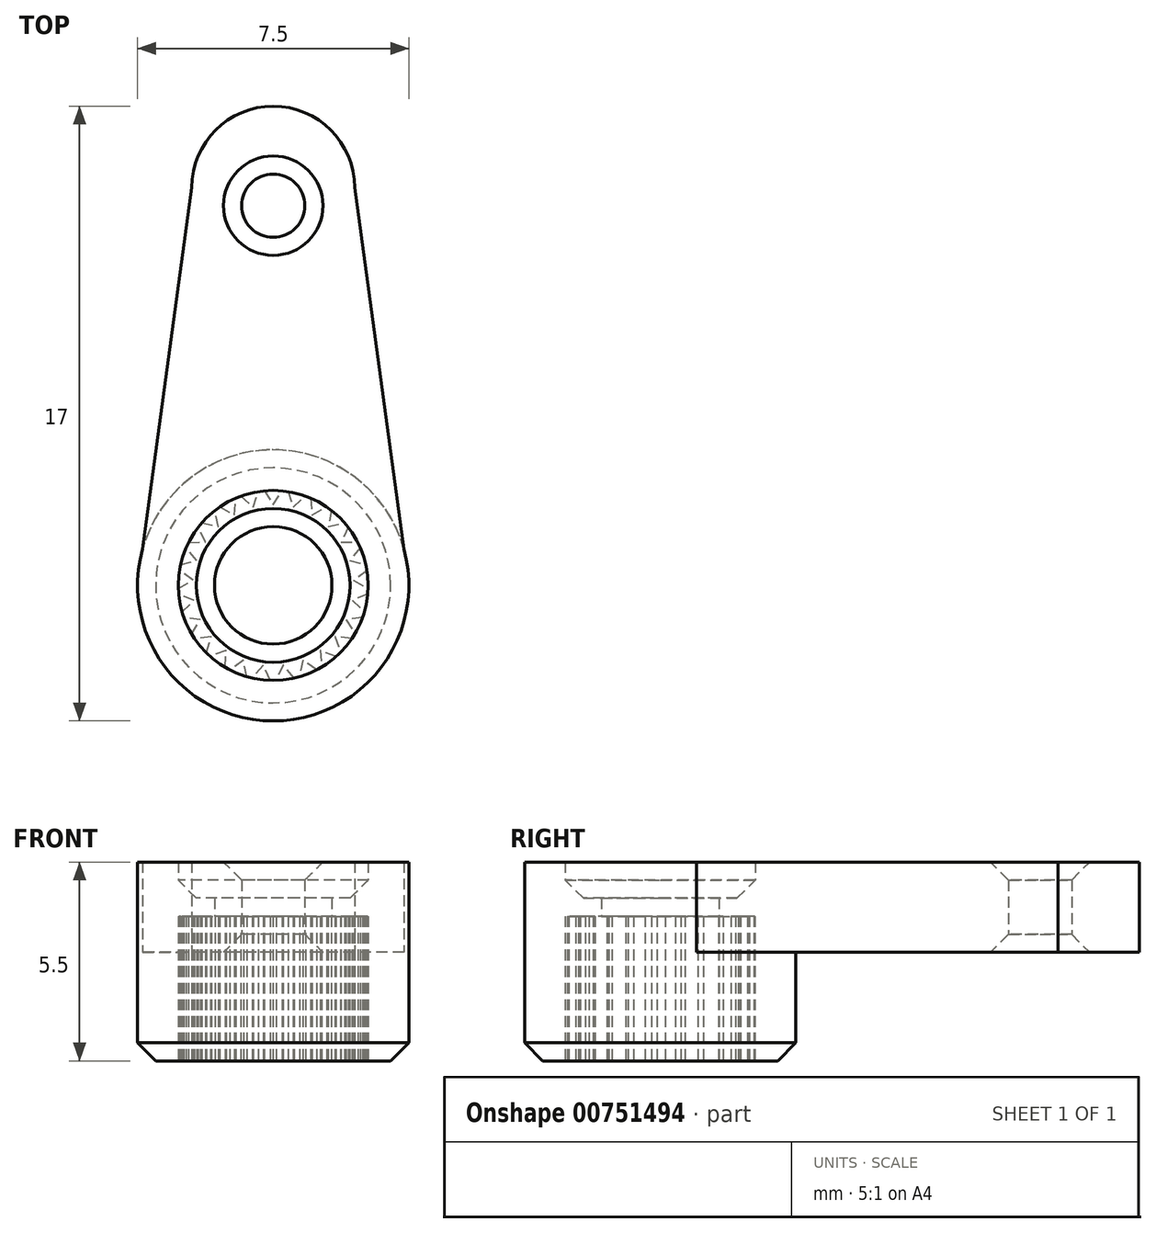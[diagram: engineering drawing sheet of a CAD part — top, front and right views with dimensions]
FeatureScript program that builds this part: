
annotation { "Feature Type Name" : "Feature", "Feature Type Description" : "" }
export const myFeature = defineFeature(function(context is Context, id is Id, definition is map)
    precondition{}
    {
        {
            assignVariable(context, id + "F0", {"name" : "BaseHeight", "anyValue" : 4});
        }
        {
            var Q0;
            Q0=qCreatedBy(makeId("Top.planeOp"),FACE);
            var sketch = newSketch(context, id + "F1", { "sketchPlane" : qUnion([Q0])});
            skCircle(sketch, "E0", {"center": v(0, 0) * mm, "radius": 2.62 * mm});
            skCircle(sketch, "E1", {"center": v(0, 0) * mm, "radius": 3.75 * mm});
            skLineSegment(sketch, "E2", {"start": v(-0.25, 2.61) * mm, "end": v(0, 2.23) * mm});
            skLineSegment(sketch, "E3", {"start": v(0, 2.23) * mm, "end": v(0.25, 2.61) * mm});
            skLineSegment(sketch, "E4.1.0", {"start": v(-0.55, 2.16) * mm, "end": v(-0.4, 2.6) * mm});
            skLineSegment(sketch, "E4.1.1", {"start": v(-0.9, 2.47) * mm, "end": v(-0.55, 2.16) * mm});
            skLineSegment(sketch, "E4.2.0", {"start": v(-1.07, 1.95) * mm, "end": v(-1.04, 2.41) * mm});
            skLineSegment(sketch, "E4.2.1", {"start": v(-1.48, 2.17) * mm, "end": v(-1.07, 1.95) * mm});
            skLineSegment(sketch, "E4.3.0", {"start": v(-1.52, 1.62) * mm, "end": v(-1.6, 2.08) * mm});
            skLineSegment(sketch, "E4.3.1", {"start": v(-1.97, 1.73) * mm, "end": v(-1.52, 1.62) * mm});
            skLineSegment(sketch, "E4.4.0", {"start": v(-1.88, 1.2) * mm, "end": v(-2.07, 1.61) * mm});
            skLineSegment(sketch, "E4.4.1", {"start": v(-2.34, 1.19) * mm, "end": v(-1.88, 1.2) * mm});
            skLineSegment(sketch, "E4.5.0", {"start": v(-2.12, 0.69) * mm, "end": v(-2.4, 1.05) * mm});
            skLineSegment(sketch, "E4.5.1", {"start": v(-2.56, 0.57) * mm, "end": v(-2.12, 0.69) * mm});
            skLineSegment(sketch, "E4.6.0", {"start": v(-2.22, 0.14) * mm, "end": v(-2.6, 0.41) * mm});
            skLineSegment(sketch, "E4.6.1", {"start": v(-2.62, -0.09) * mm, "end": v(-2.22, 0.14) * mm});
            skLineSegment(sketch, "E4.7.0", {"start": v(-2.19, -0.42) * mm, "end": v(-2.61, -0.24) * mm});
            skLineSegment(sketch, "E4.7.1", {"start": v(-2.52, -0.74) * mm, "end": v(-2.19, -0.42) * mm});
            skLineSegment(sketch, "E4.8.0", {"start": v(-2.01, -0.95) * mm, "end": v(-2.47, -0.89) * mm});
            skLineSegment(sketch, "E4.8.1", {"start": v(-2.26, -1.34) * mm, "end": v(-2.01, -0.95) * mm});
            skLineSegment(sketch, "E4.9.0", {"start": v(-1.71, -1.42) * mm, "end": v(-2.17, -1.47) * mm});
            skLineSegment(sketch, "E4.9.1", {"start": v(-1.85, -1.86) * mm, "end": v(-1.71, -1.42) * mm});
            skLineSegment(sketch, "E4.10.0", {"start": v(-1.3, -1.8) * mm, "end": v(-1.74, -1.97) * mm});
            skLineSegment(sketch, "E4.10.1", {"start": v(-1.33, -2.26) * mm, "end": v(-1.3, -1.8) * mm});
            skLineSegment(sketch, "E4.11.0", {"start": v(-0.82, -2.07) * mm, "end": v(-1.2, -2.34) * mm});
            skLineSegment(sketch, "E4.11.1", {"start": v(-0.73, -2.52) * mm, "end": v(-0.82, -2.07) * mm});
            skLineSegment(sketch, "E4.12.0", {"start": v(-0.28, -2.2) * mm, "end": v(-0.58, -2.56) * mm});
            skLineSegment(sketch, "E4.12.1", {"start": v(-0.08, -2.62) * mm, "end": v(-0.28, -2.2) * mm});
            skLineSegment(sketch, "E4.13.0", {"start": v(0.28, -2.2) * mm, "end": v(0.08, -2.62) * mm});
            skLineSegment(sketch, "E4.13.1", {"start": v(0.58, -2.56) * mm, "end": v(0.28, -2.2) * mm});
            skLineSegment(sketch, "E4.14.0", {"start": v(0.82, -2.07) * mm, "end": v(0.73, -2.52) * mm});
            skLineSegment(sketch, "E4.14.1", {"start": v(1.2, -2.34) * mm, "end": v(0.82, -2.07) * mm});
            skLineSegment(sketch, "E4.15.0", {"start": v(1.3, -1.8) * mm, "end": v(1.33, -2.26) * mm});
            skLineSegment(sketch, "E4.15.1", {"start": v(1.74, -1.97) * mm, "end": v(1.3, -1.8) * mm});
            skLineSegment(sketch, "E4.16.0", {"start": v(1.71, -1.42) * mm, "end": v(1.85, -1.86) * mm});
            skLineSegment(sketch, "E4.16.1", {"start": v(2.17, -1.47) * mm, "end": v(1.71, -1.42) * mm});
            skLineSegment(sketch, "E4.17.0", {"start": v(2.01, -0.95) * mm, "end": v(2.26, -1.34) * mm});
            skLineSegment(sketch, "E4.17.1", {"start": v(2.47, -0.89) * mm, "end": v(2.01, -0.95) * mm});
            skLineSegment(sketch, "E4.18.0", {"start": v(2.19, -0.42) * mm, "end": v(2.52, -0.74) * mm});
            skLineSegment(sketch, "E4.18.1", {"start": v(2.61, -0.24) * mm, "end": v(2.19, -0.42) * mm});
            skLineSegment(sketch, "E4.19.0", {"start": v(2.22, 0.14) * mm, "end": v(2.62, -0.09) * mm});
            skLineSegment(sketch, "E4.19.1", {"start": v(2.6, 0.41) * mm, "end": v(2.22, 0.14) * mm});
            skLineSegment(sketch, "E4.20.0", {"start": v(2.12, 0.69) * mm, "end": v(2.56, 0.57) * mm});
            skLineSegment(sketch, "E4.20.1", {"start": v(2.4, 1.05) * mm, "end": v(2.12, 0.69) * mm});
            skLineSegment(sketch, "E4.21.0", {"start": v(1.88, 1.2) * mm, "end": v(2.34, 1.19) * mm});
            skLineSegment(sketch, "E4.21.1", {"start": v(2.07, 1.61) * mm, "end": v(1.88, 1.2) * mm});
            skLineSegment(sketch, "E4.22.0", {"start": v(1.52, 1.62) * mm, "end": v(1.97, 1.73) * mm});
            skLineSegment(sketch, "E4.22.1", {"start": v(1.6, 2.08) * mm, "end": v(1.52, 1.62) * mm});
            skLineSegment(sketch, "E4.23.0", {"start": v(1.07, 1.95) * mm, "end": v(1.48, 2.17) * mm});
            skLineSegment(sketch, "E4.23.1", {"start": v(1.04, 2.41) * mm, "end": v(1.07, 1.95) * mm});
            skLineSegment(sketch, "E4.24.0", {"start": v(0.55, 2.16) * mm, "end": v(0.9, 2.47) * mm});
            skLineSegment(sketch, "E4.24.1", {"start": v(0.4, 2.6) * mm, "end": v(0.55, 2.16) * mm});
            skCircle(sketch, "E5", {"center": v(0, 0) * mm, "radius": 1.63 * mm});
            skLineSegment(sketch, "E6", {"start": v(-3.61, 1) * mm, "end": v(-2.25, 11) * mm});
            skLineSegment(sketch, "E7", {"start": v(3.61, 1) * mm, "end": v(2.25, 11) * mm});
            skArc(sketch, "E8", {"start": v(2.25, 11) * mm, "mid": v(0, 13.25) * mm, "end": v(-2.25, 11) * mm});
            skPoint(sketch, "E9.orphan", {"position": v(-3.75, 0) * mm});
            skPoint(sketch, "E10.orphan", {"position": v(3.75, 0) * mm});
            skCircle(sketch, "E11", {"center": v(0, 10.5) * mm, "radius": 0.88 * mm});
            skSolve(sketch);
        }
        {
            var Q0;
            Q0=makeQuery(id+"F1.imprint","IMPRINT",FACE,{"disambiguationData":[TD([[makeQuery(id+"F1.imprint","IMPRINT",EDGE,{"derivedFrom":sQuery(id+"F1.wireOp",EDGE,"E0")}),-1.0]])]});
            extrude(context, id + "F2", {"entities" : qUnion([Q0]), "depth" : (getVariable(context, 'BaseHeight') + 1.5) * mm, "offsetDistance" : 25 * mm});
        }
        {
            var Q0;
            Q0=makeQuery(id+"F2.opExtrude","CAP_FACE",FACE,{"disambiguationData":[OSD([sQuery(id+"F1.wireOp",EDGE,"E0"),sQuery(id+"F1.wireOp",EDGE,"E1")])],"isStart":true});
            var Q1;
            {var subQ0=sQuery(id+"F1.wireOp",EDGE,"0f8284f6-a0f2-4ead-9c26-bed78ff55800.22.0");Q1=makeQuery(id+"F1.imprint","IMPRINT",FACE,{"disambiguationData":[TD([[makeQuery(id+"F1.imprint","IMPRINT",EDGE,{"derivedFrom":subQ0}),1.0]])]});}
            var Q2;
            {var subQ0=sQuery(id+"F1.wireOp",EDGE,"0f8284f6-a0f2-4ead-9c26-bed78ff55800.17.0");Q2=makeQuery(id+"F1.imprint","IMPRINT",FACE,{"disambiguationData":[TD([[makeQuery(id+"F1.imprint","IMPRINT",EDGE,{"derivedFrom":subQ0}),1.0]])]});}
            var Q3;
            {var subQ0=sQuery(id+"F1.wireOp",EDGE,"0f8284f6-a0f2-4ead-9c26-bed78ff55800.10.0");Q3=makeQuery(id+"F1.imprint","IMPRINT",FACE,{"disambiguationData":[TD([[makeQuery(id+"F1.imprint","IMPRINT",EDGE,{"derivedFrom":subQ0}),1.0]])]});}
            var Q4;
            {var subQ0=sQuery(id+"F1.wireOp",EDGE,"0f8284f6-a0f2-4ead-9c26-bed78ff55800.14.0");Q4=makeQuery(id+"F1.imprint","IMPRINT",FACE,{"disambiguationData":[TD([[makeQuery(id+"F1.imprint","IMPRINT",EDGE,{"derivedFrom":subQ0}),1.0]])]});}
            var Q5;
            {var subQ0=sQuery(id+"F1.wireOp",EDGE,"0f8284f6-a0f2-4ead-9c26-bed78ff55800.8.0");Q5=makeQuery(id+"F1.imprint","IMPRINT",FACE,{"disambiguationData":[TD([[makeQuery(id+"F1.imprint","IMPRINT",EDGE,{"derivedFrom":subQ0}),1.0]])]});}
            var Q6;
            {var subQ0=sQuery(id+"F1.wireOp",EDGE,"0f8284f6-a0f2-4ead-9c26-bed78ff55800.6.0");Q6=makeQuery(id+"F1.imprint","IMPRINT",FACE,{"disambiguationData":[TD([[makeQuery(id+"F1.imprint","IMPRINT",EDGE,{"derivedFrom":subQ0}),1.0]])]});}
            var Q7;
            {var subQ0=sQuery(id+"F1.wireOp",EDGE,"0f8284f6-a0f2-4ead-9c26-bed78ff55800.21.0");Q7=makeQuery(id+"F1.imprint","IMPRINT",FACE,{"disambiguationData":[TD([[makeQuery(id+"F1.imprint","IMPRINT",EDGE,{"derivedFrom":subQ0}),1.0]])]});}
            var Q8;
            {var subQ0=sQuery(id+"F1.wireOp",EDGE,"0f8284f6-a0f2-4ead-9c26-bed78ff55800.23.0");Q8=makeQuery(id+"F1.imprint","IMPRINT",FACE,{"disambiguationData":[TD([[makeQuery(id+"F1.imprint","IMPRINT",EDGE,{"derivedFrom":subQ0}),1.0]])]});}
            var Q9;
            {var subQ0=sQuery(id+"F1.wireOp",EDGE,"0f8284f6-a0f2-4ead-9c26-bed78ff55800.24.0");Q9=makeQuery(id+"F1.imprint","IMPRINT",FACE,{"disambiguationData":[TD([[makeQuery(id+"F1.imprint","IMPRINT",EDGE,{"derivedFrom":subQ0}),1.0]])]});}
            var Q10;
            {var subQ0=sQuery(id+"F1.wireOp",EDGE,"E2");Q10=makeQuery(id+"F1.imprint","IMPRINT",FACE,{"disambiguationData":[TD([[makeQuery(id+"F1.imprint","IMPRINT",EDGE,{"derivedFrom":subQ0}),1.0]])]});}
            var Q11;
            {var subQ0=sQuery(id+"F1.wireOp",EDGE,"0f8284f6-a0f2-4ead-9c26-bed78ff55800.2.0");Q11=makeQuery(id+"F1.imprint","IMPRINT",FACE,{"disambiguationData":[TD([[makeQuery(id+"F1.imprint","IMPRINT",EDGE,{"derivedFrom":subQ0}),1.0]])]});}
            var Q12;
            {var subQ0=sQuery(id+"F1.wireOp",EDGE,"0f8284f6-a0f2-4ead-9c26-bed78ff55800.3.0");Q12=makeQuery(id+"F1.imprint","IMPRINT",FACE,{"disambiguationData":[TD([[makeQuery(id+"F1.imprint","IMPRINT",EDGE,{"derivedFrom":subQ0}),1.0]])]});}
            var Q13;
            {var subQ0=sQuery(id+"F1.wireOp",EDGE,"0f8284f6-a0f2-4ead-9c26-bed78ff55800.4.0");Q13=makeQuery(id+"F1.imprint","IMPRINT",FACE,{"disambiguationData":[TD([[makeQuery(id+"F1.imprint","IMPRINT",EDGE,{"derivedFrom":subQ0}),1.0]])]});}
            var Q14;
            {var subQ0=sQuery(id+"F1.wireOp",EDGE,"0f8284f6-a0f2-4ead-9c26-bed78ff55800.19.0");Q14=makeQuery(id+"F1.imprint","IMPRINT",FACE,{"disambiguationData":[TD([[makeQuery(id+"F1.imprint","IMPRINT",EDGE,{"derivedFrom":subQ0}),1.0]])]});}
            var Q15;
            {var subQ0=sQuery(id+"F1.wireOp",EDGE,"0f8284f6-a0f2-4ead-9c26-bed78ff55800.15.0");Q15=makeQuery(id+"F1.imprint","IMPRINT",FACE,{"disambiguationData":[TD([[makeQuery(id+"F1.imprint","IMPRINT",EDGE,{"derivedFrom":subQ0}),1.0]])]});}
            var Q16;
            {var subQ0=sQuery(id+"F1.wireOp",EDGE,"0f8284f6-a0f2-4ead-9c26-bed78ff55800.13.0");Q16=makeQuery(id+"F1.imprint","IMPRINT",FACE,{"disambiguationData":[TD([[makeQuery(id+"F1.imprint","IMPRINT",EDGE,{"derivedFrom":subQ0}),1.0]])]});}
            var Q17;
            {var subQ0=sQuery(id+"F1.wireOp",EDGE,"0f8284f6-a0f2-4ead-9c26-bed78ff55800.18.0");Q17=makeQuery(id+"F1.imprint","IMPRINT",FACE,{"disambiguationData":[TD([[makeQuery(id+"F1.imprint","IMPRINT",EDGE,{"derivedFrom":subQ0}),1.0]])]});}
            var Q18;
            {var subQ0=sQuery(id+"F1.wireOp",EDGE,"0f8284f6-a0f2-4ead-9c26-bed78ff55800.12.0");Q18=makeQuery(id+"F1.imprint","IMPRINT",FACE,{"disambiguationData":[TD([[makeQuery(id+"F1.imprint","IMPRINT",EDGE,{"derivedFrom":subQ0}),1.0]])]});}
            var Q19;
            {var subQ0=sQuery(id+"F1.wireOp",EDGE,"0f8284f6-a0f2-4ead-9c26-bed78ff55800.7.0");Q19=makeQuery(id+"F1.imprint","IMPRINT",FACE,{"disambiguationData":[TD([[makeQuery(id+"F1.imprint","IMPRINT",EDGE,{"derivedFrom":subQ0}),1.0]])]});}
            var Q20;
            {var subQ0=sQuery(id+"F1.wireOp",EDGE,"0f8284f6-a0f2-4ead-9c26-bed78ff55800.5.0");Q20=makeQuery(id+"F1.imprint","IMPRINT",FACE,{"disambiguationData":[TD([[makeQuery(id+"F1.imprint","IMPRINT",EDGE,{"derivedFrom":subQ0}),1.0]])]});}
            var Q21;
            {var subQ0=sQuery(id+"F1.wireOp",EDGE,"0f8284f6-a0f2-4ead-9c26-bed78ff55800.20.0");Q21=makeQuery(id+"F1.imprint","IMPRINT",FACE,{"disambiguationData":[TD([[makeQuery(id+"F1.imprint","IMPRINT",EDGE,{"derivedFrom":subQ0}),1.0]])]});}
            var Q22;
            {var subQ0=sQuery(id+"F1.wireOp",EDGE,"0f8284f6-a0f2-4ead-9c26-bed78ff55800.1.0");Q22=makeQuery(id+"F1.imprint","IMPRINT",FACE,{"disambiguationData":[TD([[makeQuery(id+"F1.imprint","IMPRINT",EDGE,{"derivedFrom":subQ0}),1.0]])]});}
            var Q23;
            {var subQ0=sQuery(id+"F1.wireOp",EDGE,"0f8284f6-a0f2-4ead-9c26-bed78ff55800.9.0");Q23=makeQuery(id+"F1.imprint","IMPRINT",FACE,{"disambiguationData":[TD([[makeQuery(id+"F1.imprint","IMPRINT",EDGE,{"derivedFrom":subQ0}),1.0]])]});}
            var Q24;
            {var subQ0=sQuery(id+"F1.wireOp",EDGE,"0f8284f6-a0f2-4ead-9c26-bed78ff55800.16.0");Q24=makeQuery(id+"F1.imprint","IMPRINT",FACE,{"disambiguationData":[TD([[makeQuery(id+"F1.imprint","IMPRINT",EDGE,{"derivedFrom":subQ0}),1.0]])]});}
            var Q25;
            {var subQ0=sQuery(id+"F1.wireOp",EDGE,"0f8284f6-a0f2-4ead-9c26-bed78ff55800.11.0");Q25=makeQuery(id+"F1.imprint","IMPRINT",FACE,{"disambiguationData":[TD([[makeQuery(id+"F1.imprint","IMPRINT",EDGE,{"derivedFrom":subQ0}),1.0]])]});}
            var Q26;
            {var subQ22=sQuery(id+"F1.wireOp",EDGE,"E2");Q26=makeQuery(id+"F1.imprint","IMPRINT",FACE,{"disambiguationData":[TD([[makeQuery(id+"F1.imprint","IMPRINT",EDGE,{"derivedFrom":subQ22}),-1.0]])]});}
            var Q27;
            {var subQ0=sQuery(id+"F1.wireOp",EDGE,"E4.21.0");Q27=makeQuery(id+"F1.imprint","IMPRINT",FACE,{"disambiguationData":[TD([[makeQuery(id+"F1.imprint","IMPRINT",EDGE,{"derivedFrom":subQ0}),1.0]])]});}
            var Q28;
            {var subQ0=sQuery(id+"F1.wireOp",EDGE,"E4.20.0");Q28=makeQuery(id+"F1.imprint","IMPRINT",FACE,{"disambiguationData":[TD([[makeQuery(id+"F1.imprint","IMPRINT",EDGE,{"derivedFrom":subQ0}),1.0]])]});}
            var Q29;
            {var subQ0=sQuery(id+"F1.wireOp",EDGE,"E4.19.0");Q29=makeQuery(id+"F1.imprint","IMPRINT",FACE,{"disambiguationData":[TD([[makeQuery(id+"F1.imprint","IMPRINT",EDGE,{"derivedFrom":subQ0}),1.0]])]});}
            var Q30;
            {var subQ0=sQuery(id+"F1.wireOp",EDGE,"E4.18.0");Q30=makeQuery(id+"F1.imprint","IMPRINT",FACE,{"disambiguationData":[TD([[makeQuery(id+"F1.imprint","IMPRINT",EDGE,{"derivedFrom":subQ0}),1.0]])]});}
            var Q31;
            {var subQ0=sQuery(id+"F1.wireOp",EDGE,"E4.17.0");Q31=makeQuery(id+"F1.imprint","IMPRINT",FACE,{"disambiguationData":[TD([[makeQuery(id+"F1.imprint","IMPRINT",EDGE,{"derivedFrom":subQ0}),1.0]])]});}
            var Q32;
            {var subQ0=sQuery(id+"F1.wireOp",EDGE,"E4.23.0");Q32=makeQuery(id+"F1.imprint","IMPRINT",FACE,{"disambiguationData":[TD([[makeQuery(id+"F1.imprint","IMPRINT",EDGE,{"derivedFrom":subQ0}),1.0]])]});}
            var Q33;
            {var subQ0=sQuery(id+"F1.wireOp",EDGE,"E4.22.0");Q33=makeQuery(id+"F1.imprint","IMPRINT",FACE,{"disambiguationData":[TD([[makeQuery(id+"F1.imprint","IMPRINT",EDGE,{"derivedFrom":subQ0}),1.0]])]});}
            var Q34;
            {var subQ0=sQuery(id+"F1.wireOp",EDGE,"E4.24.0");Q34=makeQuery(id+"F1.imprint","IMPRINT",FACE,{"disambiguationData":[TD([[makeQuery(id+"F1.imprint","IMPRINT",EDGE,{"derivedFrom":subQ0}),1.0]])]});}
            var Q35;
            {var subQ0=sQuery(id+"F1.wireOp",EDGE,"E4.1.0");Q35=makeQuery(id+"F1.imprint","IMPRINT",FACE,{"disambiguationData":[TD([[makeQuery(id+"F1.imprint","IMPRINT",EDGE,{"derivedFrom":subQ0}),1.0]])]});}
            var Q36;
            {var subQ0=sQuery(id+"F1.wireOp",EDGE,"E4.2.0");Q36=makeQuery(id+"F1.imprint","IMPRINT",FACE,{"disambiguationData":[TD([[makeQuery(id+"F1.imprint","IMPRINT",EDGE,{"derivedFrom":subQ0}),1.0]])]});}
            var Q37;
            {var subQ0=sQuery(id+"F1.wireOp",EDGE,"E4.3.0");Q37=makeQuery(id+"F1.imprint","IMPRINT",FACE,{"disambiguationData":[TD([[makeQuery(id+"F1.imprint","IMPRINT",EDGE,{"derivedFrom":subQ0}),1.0]])]});}
            var Q38;
            {var subQ0=sQuery(id+"F1.wireOp",EDGE,"E4.4.0");Q38=makeQuery(id+"F1.imprint","IMPRINT",FACE,{"disambiguationData":[TD([[makeQuery(id+"F1.imprint","IMPRINT",EDGE,{"derivedFrom":subQ0}),1.0]])]});}
            var Q39;
            {var subQ0=sQuery(id+"F1.wireOp",EDGE,"E4.5.0");Q39=makeQuery(id+"F1.imprint","IMPRINT",FACE,{"disambiguationData":[TD([[makeQuery(id+"F1.imprint","IMPRINT",EDGE,{"derivedFrom":subQ0}),1.0]])]});}
            var Q40;
            {var subQ0=sQuery(id+"F1.wireOp",EDGE,"E4.6.0");Q40=makeQuery(id+"F1.imprint","IMPRINT",FACE,{"disambiguationData":[TD([[makeQuery(id+"F1.imprint","IMPRINT",EDGE,{"derivedFrom":subQ0}),1.0]])]});}
            var Q41;
            {var subQ0=sQuery(id+"F1.wireOp",EDGE,"E4.7.0");Q41=makeQuery(id+"F1.imprint","IMPRINT",FACE,{"disambiguationData":[TD([[makeQuery(id+"F1.imprint","IMPRINT",EDGE,{"derivedFrom":subQ0}),1.0]])]});}
            var Q42;
            {var subQ0=sQuery(id+"F1.wireOp",EDGE,"E4.8.0");Q42=makeQuery(id+"F1.imprint","IMPRINT",FACE,{"disambiguationData":[TD([[makeQuery(id+"F1.imprint","IMPRINT",EDGE,{"derivedFrom":subQ0}),1.0]])]});}
            var Q43;
            {var subQ0=sQuery(id+"F1.wireOp",EDGE,"E4.9.0");Q43=makeQuery(id+"F1.imprint","IMPRINT",FACE,{"disambiguationData":[TD([[makeQuery(id+"F1.imprint","IMPRINT",EDGE,{"derivedFrom":subQ0}),1.0]])]});}
            var Q44;
            {var subQ0=sQuery(id+"F1.wireOp",EDGE,"E4.10.0");Q44=makeQuery(id+"F1.imprint","IMPRINT",FACE,{"disambiguationData":[TD([[makeQuery(id+"F1.imprint","IMPRINT",EDGE,{"derivedFrom":subQ0}),1.0]])]});}
            var Q45;
            {var subQ0=sQuery(id+"F1.wireOp",EDGE,"E4.11.0");Q45=makeQuery(id+"F1.imprint","IMPRINT",FACE,{"disambiguationData":[TD([[makeQuery(id+"F1.imprint","IMPRINT",EDGE,{"derivedFrom":subQ0}),1.0]])]});}
            var Q46;
            {var subQ0=sQuery(id+"F1.wireOp",EDGE,"E4.16.0");Q46=makeQuery(id+"F1.imprint","IMPRINT",FACE,{"disambiguationData":[TD([[makeQuery(id+"F1.imprint","IMPRINT",EDGE,{"derivedFrom":subQ0}),1.0]])]});}
            var Q47;
            {var subQ0=sQuery(id+"F1.wireOp",EDGE,"E4.15.0");Q47=makeQuery(id+"F1.imprint","IMPRINT",FACE,{"disambiguationData":[TD([[makeQuery(id+"F1.imprint","IMPRINT",EDGE,{"derivedFrom":subQ0}),1.0]])]});}
            var Q48;
            {var subQ0=sQuery(id+"F1.wireOp",EDGE,"E4.14.0");Q48=makeQuery(id+"F1.imprint","IMPRINT",FACE,{"disambiguationData":[TD([[makeQuery(id+"F1.imprint","IMPRINT",EDGE,{"derivedFrom":subQ0}),1.0]])]});}
            var Q49;
            {var subQ0=sQuery(id+"F1.wireOp",EDGE,"E4.13.0");Q49=makeQuery(id+"F1.imprint","IMPRINT",FACE,{"disambiguationData":[TD([[makeQuery(id+"F1.imprint","IMPRINT",EDGE,{"derivedFrom":subQ0}),1.0]])]});}
            var Q50;
            {var subQ0=sQuery(id+"F1.wireOp",EDGE,"E4.12.0");Q50=makeQuery(id+"F1.imprint","IMPRINT",FACE,{"disambiguationData":[TD([[makeQuery(id+"F1.imprint","IMPRINT",EDGE,{"derivedFrom":subQ0}),1.0]])]});}
            extrude(context, id + "F3", {"entities" : qUnion([Q0, Q1, Q2, Q3, Q4, Q5, Q6, Q7, Q8, Q9, Q10, Q11, Q12, Q13, Q14, Q15, Q16, Q17, Q18, Q19, Q20, Q21, Q22, Q23, Q24, Q25, Q26, Q27, Q28, Q29, Q30, Q31, Q32, Q33, Q34, Q35, Q36, Q37, Q38, Q39, Q40, Q41, Q42, Q43, Q44, Q45, Q46, Q47, Q48, Q49, Q50]), "operationType" : NewBodyOperationType.ADD, "oppositeDirection" : true, "depth" : (getVariable(context, 'BaseHeight') + .5) * mm, "offsetDistance" : 25 * mm, "hasSecondDirection" : true, "secondDirectionOppositeDirection" : true, "secondDirectionDepth" : 4 * mm});
        }
        {
            var Q0;
            Q0=makeQuery(id+"F2.opExtrude","CAP_FACE",FACE,{"disambiguationData":[OSD([sQuery(id+"F1.wireOp",EDGE,"E0"),sQuery(id+"F1.wireOp",EDGE,"E1")])],"isStart":true});
            var Q1;
            {var subQ0=sQuery(id+"F1.wireOp",EDGE,"0f8284f6-a0f2-4ead-9c26-bed78ff55800.19.0");Q1=makeQuery(id+"F1.imprint","IMPRINT",FACE,{"disambiguationData":[TD([[makeQuery(id+"F1.imprint","IMPRINT",EDGE,{"derivedFrom":subQ0}),1.0]])]});}
            var Q2;
            {var subQ0=sQuery(id+"F1.wireOp",EDGE,"0f8284f6-a0f2-4ead-9c26-bed78ff55800.10.0");Q2=makeQuery(id+"F1.imprint","IMPRINT",FACE,{"disambiguationData":[TD([[makeQuery(id+"F1.imprint","IMPRINT",EDGE,{"derivedFrom":subQ0}),1.0]])]});}
            var Q3;
            {var subQ0=sQuery(id+"F1.wireOp",EDGE,"0f8284f6-a0f2-4ead-9c26-bed78ff55800.11.0");Q3=makeQuery(id+"F1.imprint","IMPRINT",FACE,{"disambiguationData":[TD([[makeQuery(id+"F1.imprint","IMPRINT",EDGE,{"derivedFrom":subQ0}),1.0]])]});}
            var Q4;
            {var subQ0=sQuery(id+"F1.wireOp",EDGE,"0f8284f6-a0f2-4ead-9c26-bed78ff55800.12.0");Q4=makeQuery(id+"F1.imprint","IMPRINT",FACE,{"disambiguationData":[TD([[makeQuery(id+"F1.imprint","IMPRINT",EDGE,{"derivedFrom":subQ0}),1.0]])]});}
            var Q5;
            {var subQ0=sQuery(id+"F1.wireOp",EDGE,"0f8284f6-a0f2-4ead-9c26-bed78ff55800.13.0");Q5=makeQuery(id+"F1.imprint","IMPRINT",FACE,{"disambiguationData":[TD([[makeQuery(id+"F1.imprint","IMPRINT",EDGE,{"derivedFrom":subQ0}),1.0]])]});}
            var Q6;
            {var subQ0=sQuery(id+"F1.wireOp",EDGE,"0f8284f6-a0f2-4ead-9c26-bed78ff55800.15.0");Q6=makeQuery(id+"F1.imprint","IMPRINT",FACE,{"disambiguationData":[TD([[makeQuery(id+"F1.imprint","IMPRINT",EDGE,{"derivedFrom":subQ0}),1.0]])]});}
            var Q7;
            {var subQ0=sQuery(id+"F1.wireOp",EDGE,"0f8284f6-a0f2-4ead-9c26-bed78ff55800.8.0");Q7=makeQuery(id+"F1.imprint","IMPRINT",FACE,{"disambiguationData":[TD([[makeQuery(id+"F1.imprint","IMPRINT",EDGE,{"derivedFrom":subQ0}),1.0]])]});}
            var Q8;
            {var subQ0=sQuery(id+"F1.wireOp",EDGE,"0f8284f6-a0f2-4ead-9c26-bed78ff55800.7.0");Q8=makeQuery(id+"F1.imprint","IMPRINT",FACE,{"disambiguationData":[TD([[makeQuery(id+"F1.imprint","IMPRINT",EDGE,{"derivedFrom":subQ0}),1.0]])]});}
            var Q9;
            {var subQ0=sQuery(id+"F1.wireOp",EDGE,"0f8284f6-a0f2-4ead-9c26-bed78ff55800.20.0");Q9=makeQuery(id+"F1.imprint","IMPRINT",FACE,{"disambiguationData":[TD([[makeQuery(id+"F1.imprint","IMPRINT",EDGE,{"derivedFrom":subQ0}),1.0]])]});}
            var Q10;
            {var subQ0=sQuery(id+"F1.wireOp",EDGE,"0f8284f6-a0f2-4ead-9c26-bed78ff55800.21.0");Q10=makeQuery(id+"F1.imprint","IMPRINT",FACE,{"disambiguationData":[TD([[makeQuery(id+"F1.imprint","IMPRINT",EDGE,{"derivedFrom":subQ0}),1.0]])]});}
            var Q11;
            {var subQ0=sQuery(id+"F1.wireOp",EDGE,"0f8284f6-a0f2-4ead-9c26-bed78ff55800.23.0");Q11=makeQuery(id+"F1.imprint","IMPRINT",FACE,{"disambiguationData":[TD([[makeQuery(id+"F1.imprint","IMPRINT",EDGE,{"derivedFrom":subQ0}),1.0]])]});}
            var Q12;
            {var subQ0=sQuery(id+"F1.wireOp",EDGE,"E2");Q12=makeQuery(id+"F1.imprint","IMPRINT",FACE,{"disambiguationData":[TD([[makeQuery(id+"F1.imprint","IMPRINT",EDGE,{"derivedFrom":subQ0}),1.0]])]});}
            var Q13;
            {var subQ0=sQuery(id+"F1.wireOp",EDGE,"0f8284f6-a0f2-4ead-9c26-bed78ff55800.1.0");Q13=makeQuery(id+"F1.imprint","IMPRINT",FACE,{"disambiguationData":[TD([[makeQuery(id+"F1.imprint","IMPRINT",EDGE,{"derivedFrom":subQ0}),1.0]])]});}
            var Q14;
            {var subQ0=sQuery(id+"F1.wireOp",EDGE,"0f8284f6-a0f2-4ead-9c26-bed78ff55800.3.0");Q14=makeQuery(id+"F1.imprint","IMPRINT",FACE,{"disambiguationData":[TD([[makeQuery(id+"F1.imprint","IMPRINT",EDGE,{"derivedFrom":subQ0}),1.0]])]});}
            var Q15;
            {var subQ0=sQuery(id+"F1.wireOp",EDGE,"0f8284f6-a0f2-4ead-9c26-bed78ff55800.4.0");Q15=makeQuery(id+"F1.imprint","IMPRINT",FACE,{"disambiguationData":[TD([[makeQuery(id+"F1.imprint","IMPRINT",EDGE,{"derivedFrom":subQ0}),1.0]])]});}
            var Q16;
            {var subQ0=sQuery(id+"F1.wireOp",EDGE,"0f8284f6-a0f2-4ead-9c26-bed78ff55800.5.0");Q16=makeQuery(id+"F1.imprint","IMPRINT",FACE,{"disambiguationData":[TD([[makeQuery(id+"F1.imprint","IMPRINT",EDGE,{"derivedFrom":subQ0}),1.0]])]});}
            var Q17;
            {var subQ0=sQuery(id+"F1.wireOp",EDGE,"0f8284f6-a0f2-4ead-9c26-bed78ff55800.16.0");Q17=makeQuery(id+"F1.imprint","IMPRINT",FACE,{"disambiguationData":[TD([[makeQuery(id+"F1.imprint","IMPRINT",EDGE,{"derivedFrom":subQ0}),1.0]])]});}
            var Q18;
            {var subQ0=sQuery(id+"F1.wireOp",EDGE,"0f8284f6-a0f2-4ead-9c26-bed78ff55800.17.0");Q18=makeQuery(id+"F1.imprint","IMPRINT",FACE,{"disambiguationData":[TD([[makeQuery(id+"F1.imprint","IMPRINT",EDGE,{"derivedFrom":subQ0}),1.0]])]});}
            var Q19;
            {var subQ0=sQuery(id+"F1.wireOp",EDGE,"0f8284f6-a0f2-4ead-9c26-bed78ff55800.18.0");Q19=makeQuery(id+"F1.imprint","IMPRINT",FACE,{"disambiguationData":[TD([[makeQuery(id+"F1.imprint","IMPRINT",EDGE,{"derivedFrom":subQ0}),1.0]])]});}
            var Q20;
            {var subQ0=sQuery(id+"F1.wireOp",EDGE,"0f8284f6-a0f2-4ead-9c26-bed78ff55800.9.0");Q20=makeQuery(id+"F1.imprint","IMPRINT",FACE,{"disambiguationData":[TD([[makeQuery(id+"F1.imprint","IMPRINT",EDGE,{"derivedFrom":subQ0}),1.0]])]});}
            var Q21;
            {var subQ0=sQuery(id+"F1.wireOp",EDGE,"0f8284f6-a0f2-4ead-9c26-bed78ff55800.14.0");Q21=makeQuery(id+"F1.imprint","IMPRINT",FACE,{"disambiguationData":[TD([[makeQuery(id+"F1.imprint","IMPRINT",EDGE,{"derivedFrom":subQ0}),1.0]])]});}
            var Q22;
            {var subQ0=sQuery(id+"F1.wireOp",EDGE,"0f8284f6-a0f2-4ead-9c26-bed78ff55800.6.0");Q22=makeQuery(id+"F1.imprint","IMPRINT",FACE,{"disambiguationData":[TD([[makeQuery(id+"F1.imprint","IMPRINT",EDGE,{"derivedFrom":subQ0}),1.0]])]});}
            var Q23;
            {var subQ0=sQuery(id+"F1.wireOp",EDGE,"0f8284f6-a0f2-4ead-9c26-bed78ff55800.22.0");Q23=makeQuery(id+"F1.imprint","IMPRINT",FACE,{"disambiguationData":[TD([[makeQuery(id+"F1.imprint","IMPRINT",EDGE,{"derivedFrom":subQ0}),1.0]])]});}
            var Q24;
            {var subQ0=sQuery(id+"F1.wireOp",EDGE,"0f8284f6-a0f2-4ead-9c26-bed78ff55800.24.0");Q24=makeQuery(id+"F1.imprint","IMPRINT",FACE,{"disambiguationData":[TD([[makeQuery(id+"F1.imprint","IMPRINT",EDGE,{"derivedFrom":subQ0}),1.0]])]});}
            var Q25;
            {var subQ0=sQuery(id+"F1.wireOp",EDGE,"0f8284f6-a0f2-4ead-9c26-bed78ff55800.2.0");Q25=makeQuery(id+"F1.imprint","IMPRINT",FACE,{"disambiguationData":[TD([[makeQuery(id+"F1.imprint","IMPRINT",EDGE,{"derivedFrom":subQ0}),1.0]])]});}
            var Q26;
            Q26=makeQuery(id+"F1.imprint","IMPRINT",FACE,{"disambiguationData":[TD([[makeQuery(id+"F1.imprint","IMPRINT",EDGE,{"derivedFrom":sQuery(id+"F1.wireOp",EDGE,"E1")}),1.0]])]});
            var Q27;
            {var subQ0=sQuery(id+"F1.wireOp",EDGE,"E4.2.0");Q27=makeQuery(id+"F1.imprint","IMPRINT",FACE,{"disambiguationData":[TD([[makeQuery(id+"F1.imprint","IMPRINT",EDGE,{"derivedFrom":subQ0}),1.0]])]});}
            var Q28;
            {var subQ0=sQuery(id+"F1.wireOp",EDGE,"E4.3.0");Q28=makeQuery(id+"F1.imprint","IMPRINT",FACE,{"disambiguationData":[TD([[makeQuery(id+"F1.imprint","IMPRINT",EDGE,{"derivedFrom":subQ0}),1.0]])]});}
            var Q29;
            {var subQ0=sQuery(id+"F1.wireOp",EDGE,"E4.5.0");Q29=makeQuery(id+"F1.imprint","IMPRINT",FACE,{"disambiguationData":[TD([[makeQuery(id+"F1.imprint","IMPRINT",EDGE,{"derivedFrom":subQ0}),1.0]])]});}
            var Q30;
            {var subQ0=sQuery(id+"F1.wireOp",EDGE,"E4.7.0");Q30=makeQuery(id+"F1.imprint","IMPRINT",FACE,{"disambiguationData":[TD([[makeQuery(id+"F1.imprint","IMPRINT",EDGE,{"derivedFrom":subQ0}),1.0]])]});}
            var Q31;
            {var subQ0=sQuery(id+"F1.wireOp",EDGE,"E4.8.0");Q31=makeQuery(id+"F1.imprint","IMPRINT",FACE,{"disambiguationData":[TD([[makeQuery(id+"F1.imprint","IMPRINT",EDGE,{"derivedFrom":subQ0}),1.0]])]});}
            var Q32;
            {var subQ0=sQuery(id+"F1.wireOp",EDGE,"E4.9.0");Q32=makeQuery(id+"F1.imprint","IMPRINT",FACE,{"disambiguationData":[TD([[makeQuery(id+"F1.imprint","IMPRINT",EDGE,{"derivedFrom":subQ0}),1.0]])]});}
            var Q33;
            {var subQ0=sQuery(id+"F1.wireOp",EDGE,"E4.10.0");Q33=makeQuery(id+"F1.imprint","IMPRINT",FACE,{"disambiguationData":[TD([[makeQuery(id+"F1.imprint","IMPRINT",EDGE,{"derivedFrom":subQ0}),1.0]])]});}
            var Q34;
            {var subQ0=sQuery(id+"F1.wireOp",EDGE,"E4.11.0");Q34=makeQuery(id+"F1.imprint","IMPRINT",FACE,{"disambiguationData":[TD([[makeQuery(id+"F1.imprint","IMPRINT",EDGE,{"derivedFrom":subQ0}),1.0]])]});}
            var Q35;
            {var subQ0=sQuery(id+"F1.wireOp",EDGE,"E4.12.0");Q35=makeQuery(id+"F1.imprint","IMPRINT",FACE,{"disambiguationData":[TD([[makeQuery(id+"F1.imprint","IMPRINT",EDGE,{"derivedFrom":subQ0}),1.0]])]});}
            var Q36;
            {var subQ0=sQuery(id+"F1.wireOp",EDGE,"E4.13.0");Q36=makeQuery(id+"F1.imprint","IMPRINT",FACE,{"disambiguationData":[TD([[makeQuery(id+"F1.imprint","IMPRINT",EDGE,{"derivedFrom":subQ0}),1.0]])]});}
            var Q37;
            {var subQ0=sQuery(id+"F1.wireOp",EDGE,"E4.14.0");Q37=makeQuery(id+"F1.imprint","IMPRINT",FACE,{"disambiguationData":[TD([[makeQuery(id+"F1.imprint","IMPRINT",EDGE,{"derivedFrom":subQ0}),1.0]])]});}
            var Q38;
            {var subQ0=sQuery(id+"F1.wireOp",EDGE,"E4.15.0");Q38=makeQuery(id+"F1.imprint","IMPRINT",FACE,{"disambiguationData":[TD([[makeQuery(id+"F1.imprint","IMPRINT",EDGE,{"derivedFrom":subQ0}),1.0]])]});}
            var Q39;
            {var subQ0=sQuery(id+"F1.wireOp",EDGE,"E4.16.0");Q39=makeQuery(id+"F1.imprint","IMPRINT",FACE,{"disambiguationData":[TD([[makeQuery(id+"F1.imprint","IMPRINT",EDGE,{"derivedFrom":subQ0}),1.0]])]});}
            var Q40;
            {var subQ0=sQuery(id+"F1.wireOp",EDGE,"E4.17.0");Q40=makeQuery(id+"F1.imprint","IMPRINT",FACE,{"disambiguationData":[TD([[makeQuery(id+"F1.imprint","IMPRINT",EDGE,{"derivedFrom":subQ0}),1.0]])]});}
            var Q41;
            {var subQ0=sQuery(id+"F1.wireOp",EDGE,"E4.18.0");Q41=makeQuery(id+"F1.imprint","IMPRINT",FACE,{"disambiguationData":[TD([[makeQuery(id+"F1.imprint","IMPRINT",EDGE,{"derivedFrom":subQ0}),1.0]])]});}
            var Q42;
            {var subQ0=sQuery(id+"F1.wireOp",EDGE,"E4.19.0");Q42=makeQuery(id+"F1.imprint","IMPRINT",FACE,{"disambiguationData":[TD([[makeQuery(id+"F1.imprint","IMPRINT",EDGE,{"derivedFrom":subQ0}),1.0]])]});}
            var Q43;
            {var subQ0=sQuery(id+"F1.wireOp",EDGE,"E4.20.0");Q43=makeQuery(id+"F1.imprint","IMPRINT",FACE,{"disambiguationData":[TD([[makeQuery(id+"F1.imprint","IMPRINT",EDGE,{"derivedFrom":subQ0}),1.0]])]});}
            var Q44;
            {var subQ0=sQuery(id+"F1.wireOp",EDGE,"E4.21.0");Q44=makeQuery(id+"F1.imprint","IMPRINT",FACE,{"disambiguationData":[TD([[makeQuery(id+"F1.imprint","IMPRINT",EDGE,{"derivedFrom":subQ0}),1.0]])]});}
            var Q45;
            {var subQ0=sQuery(id+"F1.wireOp",EDGE,"E4.22.0");Q45=makeQuery(id+"F1.imprint","IMPRINT",FACE,{"disambiguationData":[TD([[makeQuery(id+"F1.imprint","IMPRINT",EDGE,{"derivedFrom":subQ0}),1.0]])]});}
            var Q46;
            {var subQ0=sQuery(id+"F1.wireOp",EDGE,"E4.24.0");Q46=makeQuery(id+"F1.imprint","IMPRINT",FACE,{"disambiguationData":[TD([[makeQuery(id+"F1.imprint","IMPRINT",EDGE,{"derivedFrom":subQ0}),1.0]])]});}
            var Q47;
            {var subQ0=sQuery(id+"F1.wireOp",EDGE,"E4.6.0");Q47=makeQuery(id+"F1.imprint","IMPRINT",FACE,{"disambiguationData":[TD([[makeQuery(id+"F1.imprint","IMPRINT",EDGE,{"derivedFrom":subQ0}),1.0]])]});}
            var Q48;
            {var subQ0=sQuery(id+"F1.wireOp",EDGE,"E4.4.0");Q48=makeQuery(id+"F1.imprint","IMPRINT",FACE,{"disambiguationData":[TD([[makeQuery(id+"F1.imprint","IMPRINT",EDGE,{"derivedFrom":subQ0}),1.0]])]});}
            var Q49;
            {var subQ0=sQuery(id+"F1.wireOp",EDGE,"E4.1.0");Q49=makeQuery(id+"F1.imprint","IMPRINT",FACE,{"disambiguationData":[TD([[makeQuery(id+"F1.imprint","IMPRINT",EDGE,{"derivedFrom":subQ0}),1.0]])]});}
            var Q50;
            {var subQ0=sQuery(id+"F1.wireOp",EDGE,"E4.23.0");Q50=makeQuery(id+"F1.imprint","IMPRINT",FACE,{"disambiguationData":[TD([[makeQuery(id+"F1.imprint","IMPRINT",EDGE,{"derivedFrom":subQ0}),1.0]])]});}
            var Q51;
            {var subQ0=sQuery(id+"F1.wireOp",EDGE,"E0");Q51=makeQuery(id+"F3.boolean.opBoolean","MERGE",FACE,{"derivedFrom":[makeQuery(id+"F3.opExtrude","CAP_FACE",FACE,{"disambiguationData":[OSD([subQ0,sQuery(id+"F1.wireOp",EDGE,"E4.1.0"),sQuery(id+"F1.wireOp",EDGE,"E4.1.1"),sQuery(id+"F1.wireOp",EDGE,"E4.2.0"),sQuery(id+"F1.wireOp",EDGE,"E4.2.1"),sQuery(id+"F1.wireOp",EDGE,"E4.3.0"),sQuery(id+"F1.wireOp",EDGE,"E4.3.1"),sQuery(id+"F1.wireOp",EDGE,"E4.4.0"),sQuery(id+"F1.wireOp",EDGE,"E4.4.1"),sQuery(id+"F1.wireOp",EDGE,"E4.5.0"),sQuery(id+"F1.wireOp",EDGE,"E4.5.1"),sQuery(id+"F1.wireOp",EDGE,"E4.6.0"),sQuery(id+"F1.wireOp",EDGE,"E4.6.1"),sQuery(id+"F1.wireOp",EDGE,"E4.7.0"),sQuery(id+"F1.wireOp",EDGE,"E4.7.1"),sQuery(id+"F1.wireOp",EDGE,"E4.8.0"),sQuery(id+"F1.wireOp",EDGE,"E4.8.1"),sQuery(id+"F1.wireOp",EDGE,"E4.9.0"),sQuery(id+"F1.wireOp",EDGE,"E4.9.1"),sQuery(id+"F1.wireOp",EDGE,"E4.10.0"),sQuery(id+"F1.wireOp",EDGE,"E4.10.1"),sQuery(id+"F1.wireOp",EDGE,"E4.11.0"),sQuery(id+"F1.wireOp",EDGE,"E4.11.1"),sQuery(id+"F1.wireOp",EDGE,"E4.12.0"),sQuery(id+"F1.wireOp",EDGE,"E4.12.1"),sQuery(id+"F1.wireOp",EDGE,"E4.13.0"),sQuery(id+"F1.wireOp",EDGE,"E4.13.1"),sQuery(id+"F1.wireOp",EDGE,"E4.14.0"),sQuery(id+"F1.wireOp",EDGE,"E4.14.1"),sQuery(id+"F1.wireOp",EDGE,"E4.15.0"),sQuery(id+"F1.wireOp",EDGE,"E4.15.1"),sQuery(id+"F1.wireOp",EDGE,"E4.16.0"),sQuery(id+"F1.wireOp",EDGE,"E4.16.1"),sQuery(id+"F1.wireOp",EDGE,"E4.17.0"),sQuery(id+"F1.wireOp",EDGE,"E4.17.1"),sQuery(id+"F1.wireOp",EDGE,"E4.18.0"),sQuery(id+"F1.wireOp",EDGE,"E4.18.1"),sQuery(id+"F1.wireOp",EDGE,"E4.19.0"),sQuery(id+"F1.wireOp",EDGE,"E4.19.1"),sQuery(id+"F1.wireOp",EDGE,"E4.20.0"),sQuery(id+"F1.wireOp",EDGE,"E4.20.1"),sQuery(id+"F1.wireOp",EDGE,"E4.21.0"),sQuery(id+"F1.wireOp",EDGE,"E4.21.1"),sQuery(id+"F1.wireOp",EDGE,"E4.22.0"),sQuery(id+"F1.wireOp",EDGE,"E4.22.1"),sQuery(id+"F1.wireOp",EDGE,"E4.23.0"),sQuery(id+"F1.wireOp",EDGE,"E4.23.1"),sQuery(id+"F1.wireOp",EDGE,"E4.24.0"),sQuery(id+"F1.wireOp",EDGE,"E4.24.1")])],"isStart":true}),makeQuery(id+"F3.opExtrude","CAP_FACE",FACE,{"disambiguationData":[OSD([subQ0,sQuery(id+"F1.wireOp",EDGE,"E1")])],"isStart":true})]});}
            extrude(context, id + "F4", {"entities" : qUnion([Q0, Q1, Q2, Q3, Q4, Q5, Q6, Q7, Q8, Q9, Q10, Q11, Q12, Q13, Q14, Q15, Q16, Q17, Q18, Q19, Q20, Q21, Q22, Q23, Q24, Q25, Q26, Q27, Q28, Q29, Q30, Q31, Q32, Q33, Q34, Q35, Q36, Q37, Q38, Q39, Q40, Q41, Q42, Q43, Q44, Q45, Q46, Q47, Q48, Q49, Q50]), "operationType" : NewBodyOperationType.ADD, "endBound" : BoundingType.UP_TO_SURFACE, "oppositeDirection" : true, "depth" : 3 * mm, "endBoundEntityFace" : qUnion([Q51]), "offsetDistance" : 25 * mm});
        }
        {
            var Q0;
            {var subQ5=sQuery(id+"F1.wireOp",EDGE,"E8");Q0=makeQuery(id+"F1.imprint","IMPRINT",FACE,{"disambiguationData":[TD([[makeQuery(id+"F1.imprint","IMPRINT",EDGE,{"derivedFrom":subQ5}),1.0]])]});}
            extrude(context, id + "F5", {"entities" : qUnion([Q0]), "operationType" : NewBodyOperationType.ADD, "depth" : (getVariable(context, 'BaseHeight') + 1.5) * mm, "offsetDistance" : 25 * mm, "hasSecondDirection" : true, "secondDirectionOppositeDirection" : false, "secondDirectionDepth" : (getVariable(context, 'BaseHeight') + 1 - 2) * mm});
        }
        {
            var Q0;
            Q0=makeQuery(id+"F5.opExtrude","CAP_EDGE",EDGE,{"disambiguationData":[OSD([sQuery(id+"F1.wireOp",EDGE,"E11")])],"isStart":true});
            var Q1;
            Q1=makeQuery(id+"F5.opExtrude","CAP_EDGE",EDGE,{"disambiguationData":[OSD([sQuery(id+"F1.wireOp",EDGE,"m19csNj4-EMc1-MSbF-5uWt-q0yd2YdRSB2Z")])],"isStart":true});
            var Q2;
            Q2=makeQuery(id+"F5.opExtrude","CAP_EDGE",EDGE,{"disambiguationData":[OSD([sQuery(id+"F1.wireOp",EDGE,"m19csNj4-EMc1-MSbF-5uWt-q0yd2YdRSB2Z")])],"isStart":false});
            var Q3;
            Q3=makeQuery(id+"F5.opExtrude","CAP_EDGE",EDGE,{"disambiguationData":[OSD([sQuery(id+"F1.wireOp",EDGE,"E11")])],"isStart":false});
            var Q4;
            Q4=makeQuery(id+"F5.opExtrude","CAP_EDGE",EDGE,{"disambiguationData":[OSD([sQuery(id+"F1.wireOp",EDGE,"E1")])],"isStart":true});
            var Q5;
            {var subQ0=sQuery(id+"F1.wireOp",EDGE,"E0");Q5=makeQuery(id+"F3.boolean.opBoolean","INTERSECT",EDGE,{"derivedFrom":[makeQuery(id+"F2.opExtrude","SWEPT_FACE",FACE,{"disambiguationData":[OSD([subQ0])]}),makeQuery(id+"F3.opExtrude","CAP_FACE",FACE,{"disambiguationData":[OSD([subQ0,sQuery(id+"F1.wireOp",EDGE,"E5")])],"isStart":false}),makeQuery(id+"F3.opExtrude","CAP_FACE",FACE,{"disambiguationData":[OSD([subQ0,sQuery(id+"F1.wireOp",EDGE,"E1")])],"isStart":false})]});}
            var Q6;
            Q6=makeQuery(id+"F2.opExtrude","CAP_EDGE",EDGE,{"disambiguationData":[OSD([sQuery(id+"F1.wireOp",EDGE,"E1")])],"isStart":true});
            chamfer(context, id + "F6", {"entities" : qUnion([Q0, Q1, Q2, Q3, Q4, Q5, Q6]), "width" : .5 * mm, "tangentPropagation" : true});
        }
    });
